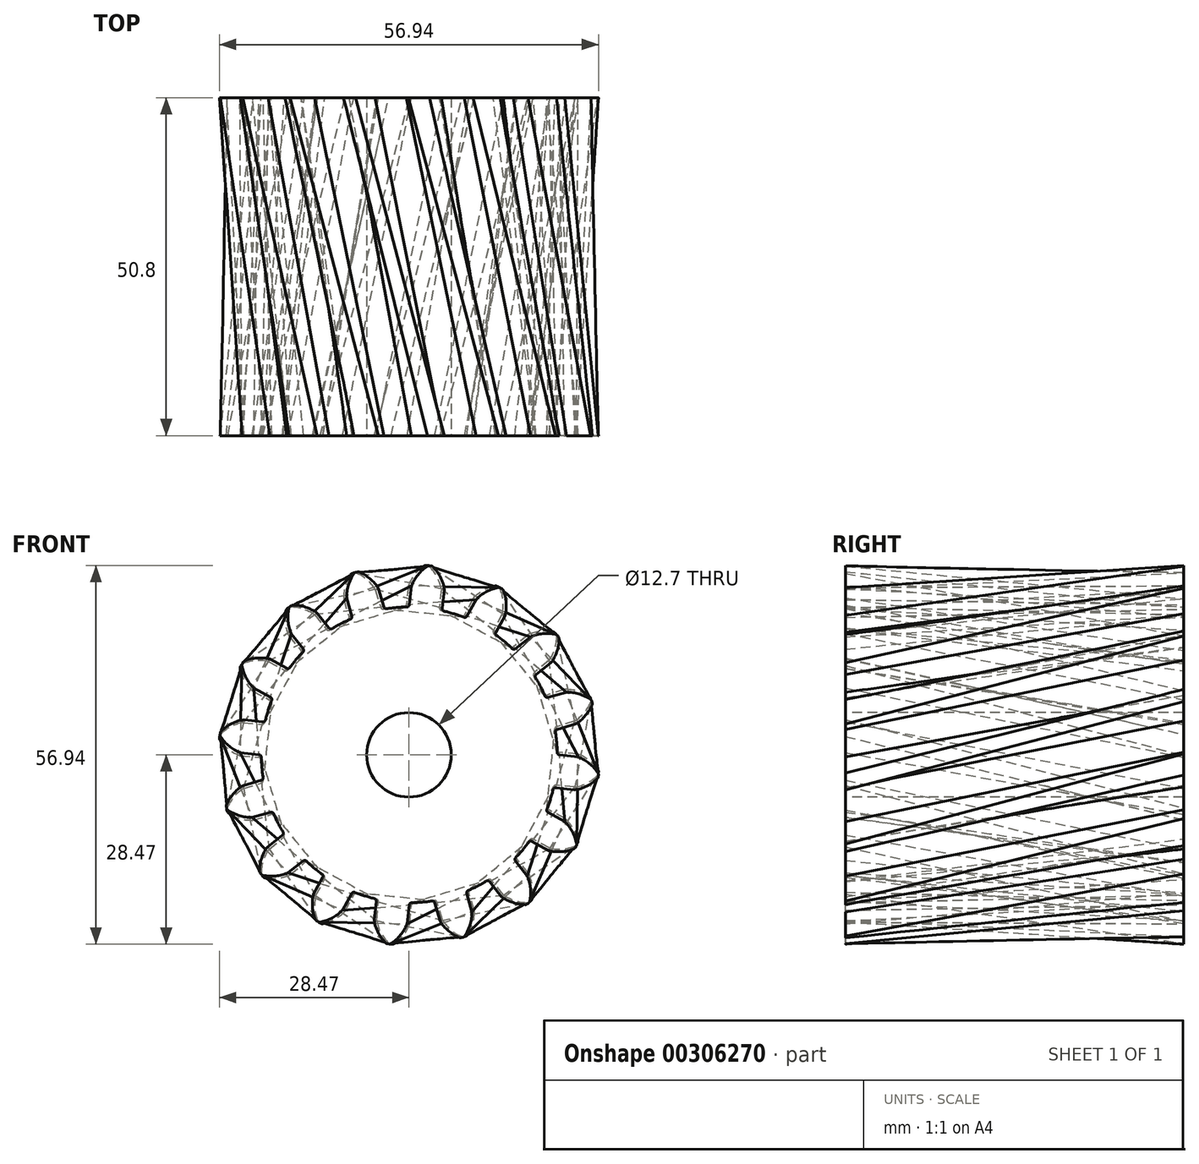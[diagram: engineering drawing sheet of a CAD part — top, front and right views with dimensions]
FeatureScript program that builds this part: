
annotation { "Feature Type Name" : "Feature", "Feature Type Description" : "" }
export const myFeature = defineFeature(function(context is Context, id is Id, definition is map)
    precondition{}
    {
        {
            var Q0;
            Q0=qCreatedBy(makeId("Front.planeOp"),FACE);
            var sketch = newSketch(context, id + "F0", { "sketchPlane" : qUnion([Q0])});
            skArc(sketch, "E0", {"start": v(-0.74, 22.21) * mm, "mid": v(-2.44, 22.1) * mm, "end": v(-4.12, 21.84) * mm});
            skArc(sketch, "E1.trimOffspring", {"start": v(4.85, 24.93) * mm, "mid": v(4.22, 26.77) * mm, "end": v(3.08, 28.32) * mm});
            skLineSegment(sketch, "E2", {"start": v(4.85, 24.93) * mm, "end": v(4.58, 22.1) * mm});
            skLineSegment(sketch, "E3", {"start": v(2.85, 28.43) * mm, "end": v(2.68, 28.45) * mm});
            skArc(sketch, "E4.MirrorCS", {"start": v(-0.11, 25.4) * mm, "mid": v(0.84, 27.08) * mm, "end": v(2.26, 28.4) * mm});
            skLineSegment(sketch, "E5.MirrorCS", {"start": v(2.5, 28.47) * mm, "end": v(2.68, 28.45) * mm});
            skLineSegment(sketch, "E6.MirrorCS", {"start": v(-0.11, 25.4) * mm, "end": v(-0.38, 22.56) * mm});
            skPoint(sketch, "E7.visualSharp", {"position": v(-0.4, 22.22) * mm});
            skArc(sketch, "E7.filletArc", {"start": v(-0.74, 22.21) * mm, "mid": v(-0.5, 22.32) * mm, "end": v(-0.38, 22.56) * mm});
            skPoint(sketch, "E8.visualSharp", {"position": v(4.55, 21.75) * mm});
            skArc(sketch, "E8.filletArc", {"start": v(4.58, 22.1) * mm, "mid": v(4.65, 21.83) * mm, "end": v(4.87, 21.68) * mm});
            skPoint(sketch, "E9.visualSharp", {"position": v(2.98, 28.42) * mm});
            skArc(sketch, "E9.filletArc", {"start": v(3.08, 28.32) * mm, "mid": v(2.97, 28.4) * mm, "end": v(2.85, 28.43) * mm});
            skPoint(sketch, "E10.visualSharp", {"position": v(2.37, 28.48) * mm});
            skArc(sketch, "E10.filletArc", {"start": v(2.5, 28.47) * mm, "mid": v(2.38, 28.45) * mm, "end": v(2.26, 28.4) * mm});
            skLineSegment(sketch, "E11.1.0", {"start": v(-9.82, 23.42) * mm, "end": v(-8.98, 20.7) * mm});
            skPoint(sketch, "E11.1.1", {"position": v(-8.88, 20.37) * mm});
            skLineSegment(sketch, "E11.1.2", {"start": v(-5.06, 24.9) * mm, "end": v(-4.22, 22.16) * mm});
            skPoint(sketch, "E11.1.3", {"position": v(-8.7, 27.22) * mm});
            skArc(sketch, "E11.1.4", {"start": v(-9.82, 23.42) * mm, "mid": v(-9.58, 25.34) * mm, "end": v(-8.78, 27.1) * mm});
            skPoint(sketch, "E11.1.5", {"position": v(-4.12, 21.84) * mm});
            skArc(sketch, "E11.1.6", {"start": v(-5.06, 24.9) * mm, "mid": v(-6.34, 26.34) * mm, "end": v(-8, 27.35) * mm});
            skPoint(sketch, "E11.1.7", {"position": v(-8.12, 27.4) * mm});
            skArc(sketch, "E11.1.8", {"start": v(-8.58, 27.26) * mm, "mid": v(-8.7, 27.2) * mm, "end": v(-8.78, 27.1) * mm});
            skLineSegment(sketch, "E11.1.9", {"start": v(-8.58, 27.26) * mm, "end": v(-8.41, 27.3) * mm});
            skArc(sketch, "E11.1.10", {"start": v(-9.19, 20.24) * mm, "mid": v(-9, 20.43) * mm, "end": v(-8.98, 20.7) * mm});
            skArc(sketch, "E11.1.11", {"start": v(-4.22, 22.16) * mm, "mid": v(-4.06, 21.95) * mm, "end": v(-3.8, 21.9) * mm});
            skLineSegment(sketch, "E11.1.12", {"start": v(-8.25, 27.36) * mm, "end": v(-8.41, 27.3) * mm});
            skArc(sketch, "E11.1.13", {"start": v(-8, 27.35) * mm, "mid": v(-8.12, 27.37) * mm, "end": v(-8.25, 27.36) * mm});
            skLineSegment(sketch, "E11.2.0", {"start": v(-18.04, 17.88) * mm, "end": v(-16.22, 15.68) * mm});
            skPoint(sketch, "E11.2.1", {"position": v(-16, 15.42) * mm});
            skLineSegment(sketch, "E11.2.2", {"start": v(-14.2, 21.06) * mm, "end": v(-12.38, 18.86) * mm});
            skPoint(sketch, "E11.2.3", {"position": v(-18.46, 21.81) * mm});
            skArc(sketch, "E11.2.4", {"start": v(-18.04, 17.88) * mm, "mid": v(-18.55, 19.75) * mm, "end": v(-18.48, 21.68) * mm});
            skPoint(sketch, "E11.2.5", {"position": v(-12.17, 18.6) * mm});
            skArc(sketch, "E11.2.6", {"start": v(-14.2, 21.06) * mm, "mid": v(-15.94, 21.91) * mm, "end": v(-17.85, 22.2) * mm});
            skPoint(sketch, "E11.2.7", {"position": v(-17.99, 22.2) * mm});
            skArc(sketch, "E11.2.8", {"start": v(-18.36, 21.9) * mm, "mid": v(-18.44, 21.8) * mm, "end": v(-18.48, 21.68) * mm});
            skLineSegment(sketch, "E11.2.9", {"start": v(-18.36, 21.9) * mm, "end": v(-18.23, 22.01) * mm});
            skArc(sketch, "E11.2.10", {"start": v(-16.23, 15.18) * mm, "mid": v(-16.13, 15.43) * mm, "end": v(-16.22, 15.68) * mm});
            skArc(sketch, "E11.2.11", {"start": v(-12.38, 18.86) * mm, "mid": v(-12.15, 18.73) * mm, "end": v(-11.89, 18.78) * mm});
            skLineSegment(sketch, "E11.2.12", {"start": v(-18.1, 22.12) * mm, "end": v(-18.23, 22.01) * mm});
            skArc(sketch, "E11.2.13", {"start": v(-17.85, 22.2) * mm, "mid": v(-17.98, 22.18) * mm, "end": v(-18.1, 22.12) * mm});
            skLineSegment(sketch, "E11.3.0", {"start": v(-23.5, 9.62) * mm, "end": v(-20.99, 8.28) * mm});
            skPoint(sketch, "E11.3.1", {"position": v(-20.69, 8.13) * mm});
            skLineSegment(sketch, "E11.3.2", {"start": v(-21.18, 14.02) * mm, "end": v(-18.66, 12.68) * mm});
            skPoint(sketch, "E11.3.3", {"position": v(-25.4, 13.1) * mm});
            skArc(sketch, "E11.3.4", {"start": v(-23.5, 9.62) * mm, "mid": v(-24.7, 11.14) * mm, "end": v(-25.37, 12.96) * mm});
            skPoint(sketch, "E11.3.5", {"position": v(-18.36, 12.53) * mm});
            skArc(sketch, "E11.3.6", {"start": v(-21.18, 14.02) * mm, "mid": v(-23.11, 14.14) * mm, "end": v(-25, 13.68) * mm});
            skPoint(sketch, "E11.3.7", {"position": v(-25.12, 13.63) * mm});
            skArc(sketch, "E11.3.8", {"start": v(-25.34, 13.2) * mm, "mid": v(-25.38, 13.09) * mm, "end": v(-25.37, 12.96) * mm});
            skLineSegment(sketch, "E11.3.9", {"start": v(-25.34, 13.2) * mm, "end": v(-25.26, 13.36) * mm});
            skArc(sketch, "E11.3.10", {"start": v(-20.8, 7.81) * mm, "mid": v(-20.8, 8.08) * mm, "end": v(-20.99, 8.28) * mm});
            skArc(sketch, "E11.3.11", {"start": v(-18.66, 12.68) * mm, "mid": v(-18.4, 12.65) * mm, "end": v(-18.17, 12.8) * mm});
            skLineSegment(sketch, "E11.3.12", {"start": v(-25.18, 13.51) * mm, "end": v(-25.26, 13.36) * mm});
            skArc(sketch, "E11.3.13", {"start": v(-25, 13.68) * mm, "mid": v(-25.1, 13.61) * mm, "end": v(-25.18, 13.51) * mm});
            skLineSegment(sketch, "E11.4.0", {"start": v(-25.4, -0.11) * mm, "end": v(-22.56, -0.38) * mm});
            skPoint(sketch, "E11.4.1", {"position": v(-22.22, -0.4) * mm});
            skLineSegment(sketch, "E11.4.2", {"start": v(-24.93, 4.85) * mm, "end": v(-22.1, 4.58) * mm});
            skPoint(sketch, "E11.4.3", {"position": v(-28.48, 2.37) * mm});
            skArc(sketch, "E11.4.4", {"start": v(-25.4, -0.11) * mm, "mid": v(-27.08, 0.84) * mm, "end": v(-28.4, 2.26) * mm});
            skPoint(sketch, "E11.4.5", {"position": v(-21.75, 4.55) * mm});
            skArc(sketch, "E11.4.6", {"start": v(-24.93, 4.85) * mm, "mid": v(-26.77, 4.22) * mm, "end": v(-28.32, 3.08) * mm});
            skPoint(sketch, "E11.4.7", {"position": v(-28.42, 2.98) * mm});
            skArc(sketch, "E11.4.8", {"start": v(-28.47, 2.5) * mm, "mid": v(-28.45, 2.38) * mm, "end": v(-28.4, 2.26) * mm});
            skLineSegment(sketch, "E11.4.9", {"start": v(-28.47, 2.5) * mm, "end": v(-28.45, 2.68) * mm});
            skArc(sketch, "E11.4.10", {"start": v(-22.21, -0.74) * mm, "mid": v(-22.32, -0.5) * mm, "end": v(-22.56, -0.38) * mm});
            skArc(sketch, "E11.4.11", {"start": v(-22.1, 4.58) * mm, "mid": v(-21.83, 4.65) * mm, "end": v(-21.68, 4.87) * mm});
            skLineSegment(sketch, "E11.4.12", {"start": v(-28.43, 2.85) * mm, "end": v(-28.45, 2.68) * mm});
            skArc(sketch, "E11.4.13", {"start": v(-28.32, 3.08) * mm, "mid": v(-28.4, 2.97) * mm, "end": v(-28.43, 2.85) * mm});
            skLineSegment(sketch, "E11.5.0", {"start": v(-23.42, -9.82) * mm, "end": v(-20.7, -8.98) * mm});
            skPoint(sketch, "E11.5.1", {"position": v(-20.37, -8.88) * mm});
            skLineSegment(sketch, "E11.5.2", {"start": v(-24.9, -5.06) * mm, "end": v(-22.16, -4.22) * mm});
            skPoint(sketch, "E11.5.3", {"position": v(-27.22, -8.7) * mm});
            skArc(sketch, "E11.5.4", {"start": v(-23.42, -9.82) * mm, "mid": v(-25.34, -9.58) * mm, "end": v(-27.1, -8.78) * mm});
            skPoint(sketch, "E11.5.5", {"position": v(-21.84, -4.12) * mm});
            skArc(sketch, "E11.5.6", {"start": v(-24.9, -5.06) * mm, "mid": v(-26.34, -6.34) * mm, "end": v(-27.35, -8) * mm});
            skPoint(sketch, "E11.5.7", {"position": v(-27.4, -8.12) * mm});
            skArc(sketch, "E11.5.8", {"start": v(-27.26, -8.58) * mm, "mid": v(-27.2, -8.7) * mm, "end": v(-27.1, -8.78) * mm});
            skLineSegment(sketch, "E11.5.9", {"start": v(-27.26, -8.58) * mm, "end": v(-27.3, -8.41) * mm});
            skArc(sketch, "E11.5.10", {"start": v(-20.24, -9.19) * mm, "mid": v(-20.43, -9) * mm, "end": v(-20.7, -8.98) * mm});
            skArc(sketch, "E11.5.11", {"start": v(-22.16, -4.22) * mm, "mid": v(-21.95, -4.06) * mm, "end": v(-21.9, -3.8) * mm});
            skLineSegment(sketch, "E11.5.12", {"start": v(-27.36, -8.25) * mm, "end": v(-27.3, -8.41) * mm});
            skArc(sketch, "E11.5.13", {"start": v(-27.35, -8) * mm, "mid": v(-27.37, -8.12) * mm, "end": v(-27.36, -8.25) * mm});
            skLineSegment(sketch, "E11.6.0", {"start": v(-17.88, -18.04) * mm, "end": v(-15.68, -16.22) * mm});
            skPoint(sketch, "E11.6.1", {"position": v(-15.42, -16) * mm});
            skLineSegment(sketch, "E11.6.2", {"start": v(-21.06, -14.2) * mm, "end": v(-18.86, -12.38) * mm});
            skPoint(sketch, "E11.6.3", {"position": v(-21.81, -18.46) * mm});
            skArc(sketch, "E11.6.4", {"start": v(-17.88, -18.04) * mm, "mid": v(-19.75, -18.55) * mm, "end": v(-21.68, -18.48) * mm});
            skPoint(sketch, "E11.6.5", {"position": v(-18.6, -12.17) * mm});
            skArc(sketch, "E11.6.6", {"start": v(-21.06, -14.2) * mm, "mid": v(-21.91, -15.94) * mm, "end": v(-22.2, -17.85) * mm});
            skPoint(sketch, "E11.6.7", {"position": v(-22.2, -17.99) * mm});
            skArc(sketch, "E11.6.8", {"start": v(-21.9, -18.36) * mm, "mid": v(-21.8, -18.44) * mm, "end": v(-21.68, -18.48) * mm});
            skLineSegment(sketch, "E11.6.9", {"start": v(-21.9, -18.36) * mm, "end": v(-22.01, -18.23) * mm});
            skArc(sketch, "E11.6.10", {"start": v(-15.18, -16.23) * mm, "mid": v(-15.43, -16.13) * mm, "end": v(-15.68, -16.22) * mm});
            skArc(sketch, "E11.6.11", {"start": v(-18.86, -12.38) * mm, "mid": v(-18.73, -12.15) * mm, "end": v(-18.78, -11.89) * mm});
            skLineSegment(sketch, "E11.6.12", {"start": v(-22.12, -18.1) * mm, "end": v(-22.01, -18.23) * mm});
            skArc(sketch, "E11.6.13", {"start": v(-22.2, -17.85) * mm, "mid": v(-22.18, -17.98) * mm, "end": v(-22.12, -18.1) * mm});
            skLineSegment(sketch, "E11.7.0", {"start": v(-9.62, -23.5) * mm, "end": v(-8.28, -20.99) * mm});
            skPoint(sketch, "E11.7.1", {"position": v(-8.13, -20.69) * mm});
            skLineSegment(sketch, "E11.7.2", {"start": v(-14.02, -21.18) * mm, "end": v(-12.68, -18.66) * mm});
            skPoint(sketch, "E11.7.3", {"position": v(-13.1, -25.4) * mm});
            skArc(sketch, "E11.7.4", {"start": v(-9.62, -23.5) * mm, "mid": v(-11.14, -24.7) * mm, "end": v(-12.96, -25.37) * mm});
            skPoint(sketch, "E11.7.5", {"position": v(-12.53, -18.36) * mm});
            skArc(sketch, "E11.7.6", {"start": v(-14.02, -21.18) * mm, "mid": v(-14.14, -23.11) * mm, "end": v(-13.68, -25) * mm});
            skPoint(sketch, "E11.7.7", {"position": v(-13.63, -25.12) * mm});
            skArc(sketch, "E11.7.8", {"start": v(-13.2, -25.34) * mm, "mid": v(-13.09, -25.38) * mm, "end": v(-12.96, -25.37) * mm});
            skLineSegment(sketch, "E11.7.9", {"start": v(-13.2, -25.34) * mm, "end": v(-13.36, -25.26) * mm});
            skArc(sketch, "E11.7.10", {"start": v(-7.81, -20.8) * mm, "mid": v(-8.08, -20.8) * mm, "end": v(-8.28, -20.99) * mm});
            skArc(sketch, "E11.7.11", {"start": v(-12.68, -18.66) * mm, "mid": v(-12.65, -18.4) * mm, "end": v(-12.8, -18.17) * mm});
            skLineSegment(sketch, "E11.7.12", {"start": v(-13.51, -25.18) * mm, "end": v(-13.36, -25.26) * mm});
            skArc(sketch, "E11.7.13", {"start": v(-13.68, -25) * mm, "mid": v(-13.61, -25.1) * mm, "end": v(-13.51, -25.18) * mm});
            skLineSegment(sketch, "E11.8.0", {"start": v(0.11, -25.4) * mm, "end": v(0.38, -22.56) * mm});
            skPoint(sketch, "E11.8.1", {"position": v(0.4, -22.22) * mm});
            skLineSegment(sketch, "E11.8.2", {"start": v(-4.85, -24.93) * mm, "end": v(-4.58, -22.1) * mm});
            skPoint(sketch, "E11.8.3", {"position": v(-2.37, -28.48) * mm});
            skArc(sketch, "E11.8.4", {"start": v(0.11, -25.4) * mm, "mid": v(-0.84, -27.08) * mm, "end": v(-2.26, -28.4) * mm});
            skPoint(sketch, "E11.8.5", {"position": v(-4.55, -21.75) * mm});
            skArc(sketch, "E11.8.6", {"start": v(-4.85, -24.93) * mm, "mid": v(-4.22, -26.77) * mm, "end": v(-3.08, -28.32) * mm});
            skPoint(sketch, "E11.8.7", {"position": v(-2.98, -28.42) * mm});
            skArc(sketch, "E11.8.8", {"start": v(-2.5, -28.47) * mm, "mid": v(-2.38, -28.45) * mm, "end": v(-2.26, -28.4) * mm});
            skLineSegment(sketch, "E11.8.9", {"start": v(-2.5, -28.47) * mm, "end": v(-2.68, -28.45) * mm});
            skArc(sketch, "E11.8.10", {"start": v(0.74, -22.21) * mm, "mid": v(0.5, -22.32) * mm, "end": v(0.38, -22.56) * mm});
            skArc(sketch, "E11.8.11", {"start": v(-4.58, -22.1) * mm, "mid": v(-4.65, -21.83) * mm, "end": v(-4.87, -21.68) * mm});
            skLineSegment(sketch, "E11.8.12", {"start": v(-2.85, -28.43) * mm, "end": v(-2.68, -28.45) * mm});
            skArc(sketch, "E11.8.13", {"start": v(-3.08, -28.32) * mm, "mid": v(-2.97, -28.4) * mm, "end": v(-2.85, -28.43) * mm});
            skLineSegment(sketch, "E11.9.0", {"start": v(9.82, -23.42) * mm, "end": v(8.98, -20.7) * mm});
            skPoint(sketch, "E11.9.1", {"position": v(8.88, -20.37) * mm});
            skLineSegment(sketch, "E11.9.2", {"start": v(5.06, -24.9) * mm, "end": v(4.22, -22.16) * mm});
            skPoint(sketch, "E11.9.3", {"position": v(8.7, -27.22) * mm});
            skArc(sketch, "E11.9.4", {"start": v(9.82, -23.42) * mm, "mid": v(9.58, -25.34) * mm, "end": v(8.78, -27.1) * mm});
            skPoint(sketch, "E11.9.5", {"position": v(4.12, -21.84) * mm});
            skArc(sketch, "E11.9.6", {"start": v(5.06, -24.9) * mm, "mid": v(6.34, -26.34) * mm, "end": v(8, -27.35) * mm});
            skPoint(sketch, "E11.9.7", {"position": v(8.12, -27.4) * mm});
            skArc(sketch, "E11.9.8", {"start": v(8.58, -27.26) * mm, "mid": v(8.7, -27.2) * mm, "end": v(8.78, -27.1) * mm});
            skLineSegment(sketch, "E11.9.9", {"start": v(8.58, -27.26) * mm, "end": v(8.41, -27.3) * mm});
            skArc(sketch, "E11.9.10", {"start": v(9.19, -20.24) * mm, "mid": v(9, -20.43) * mm, "end": v(8.98, -20.7) * mm});
            skArc(sketch, "E11.9.11", {"start": v(4.22, -22.16) * mm, "mid": v(4.06, -21.95) * mm, "end": v(3.8, -21.9) * mm});
            skLineSegment(sketch, "E11.9.12", {"start": v(8.25, -27.36) * mm, "end": v(8.41, -27.3) * mm});
            skArc(sketch, "E11.9.13", {"start": v(8, -27.35) * mm, "mid": v(8.12, -27.37) * mm, "end": v(8.25, -27.36) * mm});
            skLineSegment(sketch, "E11.10.0", {"start": v(18.04, -17.88) * mm, "end": v(16.22, -15.68) * mm});
            skPoint(sketch, "E11.10.1", {"position": v(16, -15.42) * mm});
            skLineSegment(sketch, "E11.10.2", {"start": v(14.2, -21.06) * mm, "end": v(12.38, -18.86) * mm});
            skPoint(sketch, "E11.10.3", {"position": v(18.46, -21.81) * mm});
            skArc(sketch, "E11.10.4", {"start": v(18.04, -17.88) * mm, "mid": v(18.55, -19.75) * mm, "end": v(18.48, -21.68) * mm});
            skPoint(sketch, "E11.10.5", {"position": v(12.17, -18.6) * mm});
            skArc(sketch, "E11.10.6", {"start": v(14.2, -21.06) * mm, "mid": v(15.94, -21.91) * mm, "end": v(17.85, -22.2) * mm});
            skPoint(sketch, "E11.10.7", {"position": v(17.99, -22.2) * mm});
            skArc(sketch, "E11.10.8", {"start": v(18.36, -21.9) * mm, "mid": v(18.44, -21.8) * mm, "end": v(18.48, -21.68) * mm});
            skLineSegment(sketch, "E11.10.9", {"start": v(18.36, -21.9) * mm, "end": v(18.23, -22.01) * mm});
            skArc(sketch, "E11.10.10", {"start": v(16.23, -15.18) * mm, "mid": v(16.13, -15.43) * mm, "end": v(16.22, -15.68) * mm});
            skArc(sketch, "E11.10.11", {"start": v(12.38, -18.86) * mm, "mid": v(12.15, -18.73) * mm, "end": v(11.89, -18.78) * mm});
            skLineSegment(sketch, "E11.10.12", {"start": v(18.1, -22.12) * mm, "end": v(18.23, -22.01) * mm});
            skArc(sketch, "E11.10.13", {"start": v(17.85, -22.2) * mm, "mid": v(17.98, -22.18) * mm, "end": v(18.1, -22.12) * mm});
            skLineSegment(sketch, "E11.11.0", {"start": v(23.5, -9.62) * mm, "end": v(20.99, -8.28) * mm});
            skPoint(sketch, "E11.11.1", {"position": v(20.69, -8.13) * mm});
            skLineSegment(sketch, "E11.11.2", {"start": v(21.18, -14.02) * mm, "end": v(18.66, -12.68) * mm});
            skPoint(sketch, "E11.11.3", {"position": v(25.4, -13.1) * mm});
            skArc(sketch, "E11.11.4", {"start": v(23.5, -9.62) * mm, "mid": v(24.7, -11.14) * mm, "end": v(25.37, -12.96) * mm});
            skPoint(sketch, "E11.11.5", {"position": v(18.36, -12.53) * mm});
            skArc(sketch, "E11.11.6", {"start": v(21.18, -14.02) * mm, "mid": v(23.11, -14.14) * mm, "end": v(25, -13.68) * mm});
            skPoint(sketch, "E11.11.7", {"position": v(25.12, -13.63) * mm});
            skArc(sketch, "E11.11.8", {"start": v(25.34, -13.2) * mm, "mid": v(25.38, -13.09) * mm, "end": v(25.37, -12.96) * mm});
            skLineSegment(sketch, "E11.11.9", {"start": v(25.34, -13.2) * mm, "end": v(25.26, -13.36) * mm});
            skArc(sketch, "E11.11.10", {"start": v(20.8, -7.81) * mm, "mid": v(20.8, -8.08) * mm, "end": v(20.99, -8.28) * mm});
            skArc(sketch, "E11.11.11", {"start": v(18.66, -12.68) * mm, "mid": v(18.4, -12.65) * mm, "end": v(18.17, -12.8) * mm});
            skLineSegment(sketch, "E11.11.12", {"start": v(25.18, -13.51) * mm, "end": v(25.26, -13.36) * mm});
            skArc(sketch, "E11.11.13", {"start": v(25, -13.68) * mm, "mid": v(25.1, -13.61) * mm, "end": v(25.18, -13.51) * mm});
            skLineSegment(sketch, "E11.12.0", {"start": v(25.4, 0.11) * mm, "end": v(22.56, 0.38) * mm});
            skPoint(sketch, "E11.12.1", {"position": v(22.22, 0.4) * mm});
            skLineSegment(sketch, "E11.12.2", {"start": v(24.93, -4.85) * mm, "end": v(22.1, -4.58) * mm});
            skPoint(sketch, "E11.12.3", {"position": v(28.48, -2.37) * mm});
            skArc(sketch, "E11.12.4", {"start": v(25.4, 0.11) * mm, "mid": v(27.08, -0.84) * mm, "end": v(28.4, -2.26) * mm});
            skPoint(sketch, "E11.12.5", {"position": v(21.75, -4.55) * mm});
            skArc(sketch, "E11.12.6", {"start": v(24.93, -4.85) * mm, "mid": v(26.77, -4.22) * mm, "end": v(28.32, -3.08) * mm});
            skPoint(sketch, "E11.12.7", {"position": v(28.42, -2.98) * mm});
            skArc(sketch, "E11.12.8", {"start": v(28.47, -2.5) * mm, "mid": v(28.45, -2.38) * mm, "end": v(28.4, -2.26) * mm});
            skLineSegment(sketch, "E11.12.9", {"start": v(28.47, -2.5) * mm, "end": v(28.45, -2.68) * mm});
            skArc(sketch, "E11.12.10", {"start": v(22.21, 0.74) * mm, "mid": v(22.32, 0.5) * mm, "end": v(22.56, 0.38) * mm});
            skArc(sketch, "E11.12.11", {"start": v(22.1, -4.58) * mm, "mid": v(21.83, -4.65) * mm, "end": v(21.68, -4.87) * mm});
            skLineSegment(sketch, "E11.12.12", {"start": v(28.43, -2.85) * mm, "end": v(28.45, -2.68) * mm});
            skArc(sketch, "E11.12.13", {"start": v(28.32, -3.08) * mm, "mid": v(28.4, -2.97) * mm, "end": v(28.43, -2.85) * mm});
            skLineSegment(sketch, "E11.13.0", {"start": v(23.42, 9.82) * mm, "end": v(20.7, 8.98) * mm});
            skPoint(sketch, "E11.13.1", {"position": v(20.37, 8.88) * mm});
            skLineSegment(sketch, "E11.13.2", {"start": v(24.9, 5.06) * mm, "end": v(22.16, 4.22) * mm});
            skPoint(sketch, "E11.13.3", {"position": v(27.22, 8.7) * mm});
            skArc(sketch, "E11.13.4", {"start": v(23.42, 9.82) * mm, "mid": v(25.34, 9.58) * mm, "end": v(27.1, 8.78) * mm});
            skPoint(sketch, "E11.13.5", {"position": v(21.84, 4.12) * mm});
            skArc(sketch, "E11.13.6", {"start": v(24.9, 5.06) * mm, "mid": v(26.34, 6.34) * mm, "end": v(27.35, 8) * mm});
            skPoint(sketch, "E11.13.7", {"position": v(27.4, 8.12) * mm});
            skArc(sketch, "E11.13.8", {"start": v(27.26, 8.58) * mm, "mid": v(27.2, 8.7) * mm, "end": v(27.1, 8.78) * mm});
            skLineSegment(sketch, "E11.13.9", {"start": v(27.26, 8.58) * mm, "end": v(27.3, 8.41) * mm});
            skArc(sketch, "E11.13.10", {"start": v(20.24, 9.19) * mm, "mid": v(20.43, 9) * mm, "end": v(20.7, 8.98) * mm});
            skArc(sketch, "E11.13.11", {"start": v(22.16, 4.22) * mm, "mid": v(21.95, 4.06) * mm, "end": v(21.9, 3.8) * mm});
            skLineSegment(sketch, "E11.13.12", {"start": v(27.36, 8.25) * mm, "end": v(27.3, 8.41) * mm});
            skArc(sketch, "E11.13.13", {"start": v(27.35, 8) * mm, "mid": v(27.37, 8.12) * mm, "end": v(27.36, 8.25) * mm});
            skLineSegment(sketch, "E11.14.0", {"start": v(17.88, 18.04) * mm, "end": v(15.68, 16.22) * mm});
            skPoint(sketch, "E11.14.1", {"position": v(15.42, 16) * mm});
            skLineSegment(sketch, "E11.14.2", {"start": v(21.06, 14.2) * mm, "end": v(18.86, 12.38) * mm});
            skPoint(sketch, "E11.14.3", {"position": v(21.81, 18.46) * mm});
            skArc(sketch, "E11.14.4", {"start": v(17.88, 18.04) * mm, "mid": v(19.75, 18.55) * mm, "end": v(21.68, 18.48) * mm});
            skPoint(sketch, "E11.14.5", {"position": v(18.6, 12.17) * mm});
            skArc(sketch, "E11.14.6", {"start": v(21.06, 14.2) * mm, "mid": v(21.91, 15.94) * mm, "end": v(22.2, 17.85) * mm});
            skPoint(sketch, "E11.14.7", {"position": v(22.2, 17.99) * mm});
            skArc(sketch, "E11.14.8", {"start": v(21.9, 18.36) * mm, "mid": v(21.8, 18.44) * mm, "end": v(21.68, 18.48) * mm});
            skLineSegment(sketch, "E11.14.9", {"start": v(21.9, 18.36) * mm, "end": v(22.01, 18.23) * mm});
            skArc(sketch, "E11.14.10", {"start": v(15.18, 16.23) * mm, "mid": v(15.43, 16.13) * mm, "end": v(15.68, 16.22) * mm});
            skArc(sketch, "E11.14.11", {"start": v(18.86, 12.38) * mm, "mid": v(18.73, 12.15) * mm, "end": v(18.78, 11.89) * mm});
            skLineSegment(sketch, "E11.14.12", {"start": v(22.12, 18.1) * mm, "end": v(22.01, 18.23) * mm});
            skArc(sketch, "E11.14.13", {"start": v(22.2, 17.85) * mm, "mid": v(22.18, 17.98) * mm, "end": v(22.12, 18.1) * mm});
            skLineSegment(sketch, "E11.15.0", {"start": v(9.62, 23.5) * mm, "end": v(8.28, 20.99) * mm});
            skPoint(sketch, "E11.15.1", {"position": v(8.13, 20.69) * mm});
            skLineSegment(sketch, "E11.15.2", {"start": v(14.02, 21.18) * mm, "end": v(12.68, 18.66) * mm});
            skPoint(sketch, "E11.15.3", {"position": v(13.1, 25.4) * mm});
            skArc(sketch, "E11.15.4", {"start": v(9.62, 23.5) * mm, "mid": v(11.14, 24.7) * mm, "end": v(12.96, 25.37) * mm});
            skPoint(sketch, "E11.15.5", {"position": v(12.53, 18.36) * mm});
            skArc(sketch, "E11.15.6", {"start": v(14.02, 21.18) * mm, "mid": v(14.14, 23.11) * mm, "end": v(13.68, 25) * mm});
            skPoint(sketch, "E11.15.7", {"position": v(13.63, 25.12) * mm});
            skArc(sketch, "E11.15.8", {"start": v(13.2, 25.34) * mm, "mid": v(13.09, 25.38) * mm, "end": v(12.96, 25.37) * mm});
            skLineSegment(sketch, "E11.15.9", {"start": v(13.2, 25.34) * mm, "end": v(13.36, 25.26) * mm});
            skArc(sketch, "E11.15.10", {"start": v(7.81, 20.8) * mm, "mid": v(8.08, 20.8) * mm, "end": v(8.28, 20.99) * mm});
            skArc(sketch, "E11.15.11", {"start": v(12.68, 18.66) * mm, "mid": v(12.65, 18.4) * mm, "end": v(12.8, 18.17) * mm});
            skLineSegment(sketch, "E11.15.12", {"start": v(13.51, 25.18) * mm, "end": v(13.36, 25.26) * mm});
            skArc(sketch, "E11.15.13", {"start": v(13.68, 25) * mm, "mid": v(13.61, 25.1) * mm, "end": v(13.51, 25.18) * mm});
            skArc(sketch, "E12.trimOffspring", {"start": v(8.13, 20.69) * mm, "mid": v(6.52, 21.25) * mm, "end": v(4.87, 21.68) * mm});
            skArc(sketch, "E13.trimOffspring", {"start": v(-8.88, 20.37) * mm, "mid": v(-10.56, 19.55) * mm, "end": v(-12.17, 18.6) * mm});
            skArc(sketch, "E14.trimOffspring", {"start": v(15.42, 16) * mm, "mid": v(14.02, 17.24) * mm, "end": v(12.53, 18.36) * mm});
            skArc(sketch, "E15.trimOffspring", {"start": v(-16, 15.42) * mm, "mid": v(-17.24, 14.02) * mm, "end": v(-18.36, 12.53) * mm});
            skArc(sketch, "E16.trimOffspring", {"start": v(-20.69, 8.13) * mm, "mid": v(-21.25, 6.52) * mm, "end": v(-21.68, 4.87) * mm});
            skArc(sketch, "E17.trimOffspring", {"start": v(20.37, 8.88) * mm, "mid": v(19.55, 10.56) * mm, "end": v(18.6, 12.17) * mm});
            skArc(sketch, "E18.trimOffspring", {"start": v(22.22, 0.4) * mm, "mid": v(22.1, 2.27) * mm, "end": v(21.84, 4.12) * mm});
            skArc(sketch, "E19.trimOffspring", {"start": v(-22.22, -0.4) * mm, "mid": v(-22.12, -2.1) * mm, "end": v(-21.9, -3.8) * mm});
            skArc(sketch, "E20.trimOffspring", {"start": v(-20.37, -8.88) * mm, "mid": v(-19.55, -10.56) * mm, "end": v(-18.6, -12.17) * mm});
            skArc(sketch, "E21.trimOffspring", {"start": v(-8.13, -20.69) * mm, "mid": v(-6.36, -21.3) * mm, "end": v(-4.55, -21.75) * mm});
            skArc(sketch, "E22.trimOffspring", {"start": v(-15.42, -16) * mm, "mid": v(-14.02, -17.24) * mm, "end": v(-12.53, -18.36) * mm});
            skArc(sketch, "E23.trimOffspring", {"start": v(0.4, -22.22) * mm, "mid": v(2.1, -22.12) * mm, "end": v(3.8, -21.9) * mm});
            skArc(sketch, "E24.trimOffspring", {"start": v(8.88, -20.37) * mm, "mid": v(10.41, -19.63) * mm, "end": v(11.89, -18.78) * mm});
            skArc(sketch, "E25.trimOffspring", {"start": v(16, -15.42) * mm, "mid": v(17.24, -14.02) * mm, "end": v(18.36, -12.53) * mm});
            skArc(sketch, "E26.trimOffspring", {"start": v(20.69, -8.13) * mm, "mid": v(21.3, -6.36) * mm, "end": v(21.75, -4.55) * mm});
            skSolve(sketch);
        }
        {
            var Q0;
            Q0=makeQuery(id+"F0.imprint","IMPRINT",FACE,{"disambiguationData":[TD([[makeQuery(id+"F0.imprint","IMPRINT",EDGE,{"derivedFrom":sQuery(id+"F0.wireOp",EDGE,"E1.trimOffspring")}),1.0]])]});
            cPlane(context, id + "F1", {"entities" : qUnion([Q0]), "cplaneType" : CPlaneType.OFFSET, "offset" : 50.8 * mm, "width" : 152.4 * mm, "height" : 152.4 * mm});
        }
        {
            var Q0;
            Q0=qCreatedBy(id+"F1.planeOp",FACE);
            var sketch = newSketch(context, id + "F2", { "sketchPlane" : qUnion([Q0])});
            skArc(sketch, "E27", {"start": v(-15.92, 15.46) * mm, "mid": v(-17.06, 14.2) * mm, "end": v(-18.1, 12.85) * mm});
            skArc(sketch, "E28.trimOffspring", {"start": v(-13.79, 21.3) * mm, "mid": v(-15.5, 22.19) * mm, "end": v(-17.42, 22.51) * mm});
            skLineSegment(sketch, "E29", {"start": v(-13.79, 21.3) * mm, "end": v(-12, 19.07) * mm});
            skLineSegment(sketch, "E30", {"start": v(-17.66, 22.43) * mm, "end": v(-17.8, 22.33) * mm});
            skArc(sketch, "E31.MirrorCS", {"start": v(-17.68, 18.2) * mm, "mid": v(-18.16, 20.07) * mm, "end": v(-18.06, 22) * mm});
            skLineSegment(sketch, "E32.MirrorCS", {"start": v(-17.92, 22.22) * mm, "end": v(-17.8, 22.33) * mm});
            skLineSegment(sketch, "E33.MirrorCS", {"start": v(-17.68, 18.2) * mm, "end": v(-15.9, 15.96) * mm});
            skPoint(sketch, "E34.visualSharp", {"position": v(-15.68, 15.7) * mm});
            skArc(sketch, "E34.filletArc", {"start": v(-15.92, 15.46) * mm, "mid": v(-15.81, 15.7) * mm, "end": v(-15.9, 15.96) * mm});
            skPoint(sketch, "E35.visualSharp", {"position": v(-11.8, 18.8) * mm});
            skArc(sketch, "E35.filletArc", {"start": v(-12, 19.07) * mm, "mid": v(-11.77, 18.93) * mm, "end": v(-11.5, 18.98) * mm});
            skPoint(sketch, "E36.visualSharp", {"position": v(-17.55, 22.51) * mm});
            skArc(sketch, "E36.filletArc", {"start": v(-17.42, 22.51) * mm, "mid": v(-17.54, 22.5) * mm, "end": v(-17.66, 22.43) * mm});
            skPoint(sketch, "E37.visualSharp", {"position": v(-18.03, 22.13) * mm});
            skArc(sketch, "E37.filletArc", {"start": v(-17.92, 22.22) * mm, "mid": v(-18, 22.12) * mm, "end": v(-18.06, 22) * mm});
            skLineSegment(sketch, "E38.1.0", {"start": v(-23.3, 10.03) * mm, "end": v(-20.8, 8.65) * mm});
            skPoint(sketch, "E38.1.1", {"position": v(-20.5, 8.48) * mm});
            skLineSegment(sketch, "E38.1.2", {"start": v(-20.89, 14.39) * mm, "end": v(-18.39, 13) * mm});
            skPoint(sketch, "E38.1.3", {"position": v(-25.12, 13.53) * mm});
            skArc(sketch, "E38.1.4", {"start": v(-23.3, 10.03) * mm, "mid": v(-24.45, 11.57) * mm, "end": v(-25.1, 13.4) * mm});
            skPoint(sketch, "E38.1.5", {"position": v(-18.1, 12.85) * mm});
            skArc(sketch, "E38.1.6", {"start": v(-20.89, 14.39) * mm, "mid": v(-22.81, 14.55) * mm, "end": v(-24.7, 14.12) * mm});
            skPoint(sketch, "E38.1.7", {"position": v(-24.83, 14.06) * mm});
            skArc(sketch, "E38.1.8", {"start": v(-25.06, 13.65) * mm, "mid": v(-25.1, 13.53) * mm, "end": v(-25.1, 13.4) * mm});
            skLineSegment(sketch, "E38.1.9", {"start": v(-25.06, 13.65) * mm, "end": v(-24.98, 13.8) * mm});
            skArc(sketch, "E38.1.10", {"start": v(-20.62, 8.17) * mm, "mid": v(-20.62, 8.44) * mm, "end": v(-20.8, 8.65) * mm});
            skArc(sketch, "E38.1.11", {"start": v(-18.39, 13) * mm, "mid": v(-18.12, 12.97) * mm, "end": v(-17.9, 13.12) * mm});
            skLineSegment(sketch, "E38.1.12", {"start": v(-24.9, 13.95) * mm, "end": v(-24.98, 13.8) * mm});
            skArc(sketch, "E38.1.13", {"start": v(-24.7, 14.12) * mm, "mid": v(-24.81, 14.05) * mm, "end": v(-24.9, 13.95) * mm});
            skLineSegment(sketch, "E38.2.0", {"start": v(-25.35, 0.33) * mm, "end": v(-22.51, 0.02) * mm});
            skPoint(sketch, "E38.2.1", {"position": v(-22.18, -0.02) * mm});
            skLineSegment(sketch, "E38.2.2", {"start": v(-24.8, 5.28) * mm, "end": v(-21.96, 4.96) * mm});
            skPoint(sketch, "E38.2.3", {"position": v(-28.38, 2.87) * mm});
            skArc(sketch, "E38.2.4", {"start": v(-25.35, 0.33) * mm, "mid": v(-27.02, 1.32) * mm, "end": v(-28.31, 2.76) * mm});
            skPoint(sketch, "E38.2.5", {"position": v(-21.63, 4.93) * mm});
            skArc(sketch, "E38.2.6", {"start": v(-24.8, 5.28) * mm, "mid": v(-26.64, 4.69) * mm, "end": v(-28.22, 3.57) * mm});
            skPoint(sketch, "E38.2.7", {"position": v(-28.32, 3.47) * mm});
            skArc(sketch, "E38.2.8", {"start": v(-28.37, 3) * mm, "mid": v(-28.36, 2.87) * mm, "end": v(-28.31, 2.76) * mm});
            skLineSegment(sketch, "E38.2.9", {"start": v(-28.37, 3) * mm, "end": v(-28.35, 3.17) * mm});
            skArc(sketch, "E38.2.10", {"start": v(-22.18, -0.36) * mm, "mid": v(-22.27, -0.1) * mm, "end": v(-22.51, 0.02) * mm});
            skArc(sketch, "E38.2.11", {"start": v(-21.96, 4.96) * mm, "mid": v(-21.7, 5.03) * mm, "end": v(-21.55, 5.25) * mm});
            skLineSegment(sketch, "E38.2.12", {"start": v(-28.33, 3.34) * mm, "end": v(-28.35, 3.17) * mm});
            skArc(sketch, "E38.2.13", {"start": v(-28.22, 3.57) * mm, "mid": v(-28.3, 3.47) * mm, "end": v(-28.33, 3.34) * mm});
            skLineSegment(sketch, "E38.3.0", {"start": v(-23.55, -9.41) * mm, "end": v(-20.8, -8.62) * mm});
            skPoint(sketch, "E38.3.1", {"position": v(-20.48, -8.53) * mm});
            skLineSegment(sketch, "E38.3.2", {"start": v(-24.93, -4.63) * mm, "end": v(-22.19, -3.84) * mm});
            skPoint(sketch, "E38.3.3", {"position": v(-27.32, -8.23) * mm});
            skArc(sketch, "E38.3.4", {"start": v(-23.55, -9.41) * mm, "mid": v(-25.46, -9.14) * mm, "end": v(-27.2, -8.3) * mm});
            skPoint(sketch, "E38.3.5", {"position": v(-21.86, -3.74) * mm});
            skArc(sketch, "E38.3.6", {"start": v(-24.93, -4.63) * mm, "mid": v(-26.4, -5.88) * mm, "end": v(-27.43, -7.52) * mm});
            skPoint(sketch, "E38.3.7", {"position": v(-27.49, -7.64) * mm});
            skArc(sketch, "E38.3.8", {"start": v(-27.36, -8.1) * mm, "mid": v(-27.3, -8.22) * mm, "end": v(-27.2, -8.3) * mm});
            skLineSegment(sketch, "E38.3.9", {"start": v(-27.36, -8.1) * mm, "end": v(-27.4, -7.94) * mm});
            skArc(sketch, "E38.3.10", {"start": v(-20.35, -8.83) * mm, "mid": v(-20.53, -8.64) * mm, "end": v(-20.8, -8.62) * mm});
            skArc(sketch, "E38.3.11", {"start": v(-22.19, -3.84) * mm, "mid": v(-21.97, -3.67) * mm, "end": v(-21.92, -3.41) * mm});
            skLineSegment(sketch, "E38.3.12", {"start": v(-27.45, -7.77) * mm, "end": v(-27.4, -7.94) * mm});
            skArc(sketch, "E38.3.13", {"start": v(-27.43, -7.52) * mm, "mid": v(-27.46, -7.64) * mm, "end": v(-27.45, -7.77) * mm});
            skLineSegment(sketch, "E38.4.0", {"start": v(-18.15, -17.72) * mm, "end": v(-15.92, -15.94) * mm});
            skPoint(sketch, "E38.4.1", {"position": v(-15.65, -15.73) * mm});
            skLineSegment(sketch, "E38.4.2", {"start": v(-21.26, -13.83) * mm, "end": v(-19.03, -12.05) * mm});
            skPoint(sketch, "E38.4.3", {"position": v(-22.09, -18.07) * mm});
            skArc(sketch, "E38.4.4", {"start": v(-18.15, -17.72) * mm, "mid": v(-20.02, -18.2) * mm, "end": v(-21.95, -18.1) * mm});
            skPoint(sketch, "E38.4.5", {"position": v(-18.76, -11.84) * mm});
            skArc(sketch, "E38.4.6", {"start": v(-21.26, -13.83) * mm, "mid": v(-22.14, -15.55) * mm, "end": v(-22.47, -17.46) * mm});
            skPoint(sketch, "E38.4.7", {"position": v(-22.47, -17.6) * mm});
            skArc(sketch, "E38.4.8", {"start": v(-22.17, -17.97) * mm, "mid": v(-22.07, -18.06) * mm, "end": v(-21.95, -18.1) * mm});
            skLineSegment(sketch, "E38.4.9", {"start": v(-22.17, -17.97) * mm, "end": v(-22.28, -17.84) * mm});
            skArc(sketch, "E38.4.10", {"start": v(-15.41, -15.97) * mm, "mid": v(-15.66, -15.86) * mm, "end": v(-15.92, -15.94) * mm});
            skArc(sketch, "E38.4.11", {"start": v(-19.03, -12.05) * mm, "mid": v(-18.89, -11.82) * mm, "end": v(-18.94, -11.56) * mm});
            skLineSegment(sketch, "E38.4.12", {"start": v(-22.38, -17.7) * mm, "end": v(-22.28, -17.84) * mm});
            skArc(sketch, "E38.4.13", {"start": v(-22.47, -17.46) * mm, "mid": v(-22.45, -17.59) * mm, "end": v(-22.38, -17.7) * mm});
            skLineSegment(sketch, "E38.5.0", {"start": v(-9.98, -23.34) * mm, "end": v(-8.6, -20.84) * mm});
            skPoint(sketch, "E38.5.1", {"position": v(-8.44, -20.54) * mm});
            skLineSegment(sketch, "E38.5.2", {"start": v(-14.34, -20.93) * mm, "end": v(-12.96, -18.43) * mm});
            skPoint(sketch, "E38.5.3", {"position": v(-13.49, -25.17) * mm});
            skArc(sketch, "E38.5.4", {"start": v(-9.98, -23.34) * mm, "mid": v(-11.53, -24.5) * mm, "end": v(-13.35, -25.14) * mm});
            skPoint(sketch, "E38.5.5", {"position": v(-12.8, -18.14) * mm});
            skArc(sketch, "E38.5.6", {"start": v(-14.34, -20.93) * mm, "mid": v(-14.5, -22.86) * mm, "end": v(-14.07, -24.75) * mm});
            skPoint(sketch, "E38.5.7", {"position": v(-14.02, -24.87) * mm});
            skArc(sketch, "E38.5.8", {"start": v(-13.6, -25.1) * mm, "mid": v(-13.48, -25.15) * mm, "end": v(-13.35, -25.14) * mm});
            skLineSegment(sketch, "E38.5.9", {"start": v(-13.6, -25.1) * mm, "end": v(-13.75, -25.02) * mm});
            skArc(sketch, "E38.5.10", {"start": v(-8.13, -20.67) * mm, "mid": v(-8.4, -20.66) * mm, "end": v(-8.6, -20.84) * mm});
            skArc(sketch, "E38.5.11", {"start": v(-12.96, -18.43) * mm, "mid": v(-12.92, -18.17) * mm, "end": v(-13.07, -17.94) * mm});
            skLineSegment(sketch, "E38.5.12", {"start": v(-13.9, -24.94) * mm, "end": v(-13.75, -25.02) * mm});
            skArc(sketch, "E38.5.13", {"start": v(-14.07, -24.75) * mm, "mid": v(-14, -24.86) * mm, "end": v(-13.9, -24.94) * mm});
            skLineSegment(sketch, "E38.6.0", {"start": v(-0.29, -25.4) * mm, "end": v(0.03, -22.56) * mm});
            skPoint(sketch, "E38.6.1", {"position": v(0.07, -22.22) * mm});
            skLineSegment(sketch, "E38.6.2", {"start": v(-5.23, -24.84) * mm, "end": v(-4.92, -22) * mm});
            skPoint(sketch, "E38.6.3", {"position": v(-2.82, -28.43) * mm});
            skArc(sketch, "E38.6.4", {"start": v(-0.29, -25.4) * mm, "mid": v(-1.27, -27.06) * mm, "end": v(-2.7, -28.36) * mm});
            skPoint(sketch, "E38.6.5", {"position": v(-4.88, -21.67) * mm});
            skArc(sketch, "E38.6.6", {"start": v(-5.23, -24.84) * mm, "mid": v(-4.64, -26.69) * mm, "end": v(-3.52, -28.27) * mm});
            skPoint(sketch, "E38.6.7", {"position": v(-3.43, -28.36) * mm});
            skArc(sketch, "E38.6.8", {"start": v(-2.96, -28.42) * mm, "mid": v(-2.83, -28.4) * mm, "end": v(-2.7, -28.36) * mm});
            skLineSegment(sketch, "E38.6.9", {"start": v(-2.96, -28.42) * mm, "end": v(-3.13, -28.4) * mm});
            skArc(sketch, "E38.6.10", {"start": v(0.4, -22.22) * mm, "mid": v(0.15, -22.32) * mm, "end": v(0.03, -22.56) * mm});
            skArc(sketch, "E38.6.11", {"start": v(-4.92, -22) * mm, "mid": v(-4.98, -21.75) * mm, "end": v(-5.2, -21.6) * mm});
            skLineSegment(sketch, "E38.6.12", {"start": v(-3.3, -28.38) * mm, "end": v(-3.13, -28.4) * mm});
            skArc(sketch, "E38.6.13", {"start": v(-3.52, -28.27) * mm, "mid": v(-3.42, -28.34) * mm, "end": v(-3.3, -28.38) * mm});
            skLineSegment(sketch, "E38.7.0", {"start": v(9.46, -23.6) * mm, "end": v(8.67, -20.85) * mm});
            skPoint(sketch, "E38.7.1", {"position": v(8.57, -20.52) * mm});
            skLineSegment(sketch, "E38.7.2", {"start": v(4.68, -24.97) * mm, "end": v(3.88, -22.23) * mm});
            skPoint(sketch, "E38.7.3", {"position": v(8.27, -27.36) * mm});
            skArc(sketch, "E38.7.4", {"start": v(9.46, -23.6) * mm, "mid": v(9.19, -25.5) * mm, "end": v(8.35, -27.25) * mm});
            skPoint(sketch, "E38.7.5", {"position": v(3.79, -21.9) * mm});
            skArc(sketch, "E38.7.6", {"start": v(4.68, -24.97) * mm, "mid": v(5.93, -26.45) * mm, "end": v(7.56, -27.48) * mm});
            skPoint(sketch, "E38.7.7", {"position": v(7.7, -27.53) * mm});
            skArc(sketch, "E38.7.8", {"start": v(8.15, -27.4) * mm, "mid": v(8.26, -27.35) * mm, "end": v(8.35, -27.25) * mm});
            skLineSegment(sketch, "E38.7.9", {"start": v(8.15, -27.4) * mm, "end": v(7.98, -27.45) * mm});
            skArc(sketch, "E38.7.10", {"start": v(8.88, -20.4) * mm, "mid": v(8.69, -20.58) * mm, "end": v(8.67, -20.85) * mm});
            skArc(sketch, "E38.7.11", {"start": v(3.88, -22.23) * mm, "mid": v(3.72, -22.02) * mm, "end": v(3.46, -21.96) * mm});
            skLineSegment(sketch, "E38.7.12", {"start": v(7.82, -27.5) * mm, "end": v(7.98, -27.45) * mm});
            skArc(sketch, "E38.7.13", {"start": v(7.56, -27.48) * mm, "mid": v(7.69, -27.51) * mm, "end": v(7.82, -27.5) * mm});
            skLineSegment(sketch, "E38.8.0", {"start": v(17.77, -18.2) * mm, "end": v(15.99, -15.96) * mm});
            skPoint(sketch, "E38.8.1", {"position": v(15.78, -15.7) * mm});
            skLineSegment(sketch, "E38.8.2", {"start": v(13.88, -21.3) * mm, "end": v(12.1, -19.07) * mm});
            skPoint(sketch, "E38.8.3", {"position": v(18.12, -22.13) * mm});
            skArc(sketch, "E38.8.4", {"start": v(17.77, -18.2) * mm, "mid": v(18.25, -20.07) * mm, "end": v(18.15, -22) * mm});
            skPoint(sketch, "E38.8.5", {"position": v(11.89, -18.8) * mm});
            skArc(sketch, "E38.8.6", {"start": v(13.88, -21.3) * mm, "mid": v(15.6, -22.19) * mm, "end": v(17.5, -22.51) * mm});
            skPoint(sketch, "E38.8.7", {"position": v(17.65, -22.51) * mm});
            skArc(sketch, "E38.8.8", {"start": v(18.02, -22.22) * mm, "mid": v(18.1, -22.12) * mm, "end": v(18.15, -22) * mm});
            skLineSegment(sketch, "E38.8.9", {"start": v(18.02, -22.22) * mm, "end": v(17.88, -22.33) * mm});
            skArc(sketch, "E38.8.10", {"start": v(16.01, -15.46) * mm, "mid": v(15.9, -15.7) * mm, "end": v(15.99, -15.96) * mm});
            skArc(sketch, "E38.8.11", {"start": v(12.1, -19.07) * mm, "mid": v(11.87, -18.93) * mm, "end": v(11.6, -18.98) * mm});
            skLineSegment(sketch, "E38.8.12", {"start": v(17.75, -22.43) * mm, "end": v(17.88, -22.33) * mm});
            skArc(sketch, "E38.8.13", {"start": v(17.5, -22.51) * mm, "mid": v(17.64, -22.5) * mm, "end": v(17.75, -22.43) * mm});
            skLineSegment(sketch, "E38.9.0", {"start": v(23.38, -10.03) * mm, "end": v(20.88, -8.65) * mm});
            skPoint(sketch, "E38.9.1", {"position": v(20.59, -8.48) * mm});
            skLineSegment(sketch, "E38.9.2", {"start": v(20.98, -14.39) * mm, "end": v(18.48, -13) * mm});
            skPoint(sketch, "E38.9.3", {"position": v(25.21, -13.53) * mm});
            skArc(sketch, "E38.9.4", {"start": v(23.38, -10.03) * mm, "mid": v(24.55, -11.57) * mm, "end": v(25.2, -13.4) * mm});
            skPoint(sketch, "E38.9.5", {"position": v(18.18, -12.85) * mm});
            skArc(sketch, "E38.9.6", {"start": v(20.98, -14.39) * mm, "mid": v(22.9, -14.55) * mm, "end": v(24.8, -14.12) * mm});
            skPoint(sketch, "E38.9.7", {"position": v(24.92, -14.06) * mm});
            skArc(sketch, "E38.9.8", {"start": v(25.15, -13.65) * mm, "mid": v(25.2, -13.53) * mm, "end": v(25.2, -13.4) * mm});
            skLineSegment(sketch, "E38.9.9", {"start": v(25.15, -13.65) * mm, "end": v(25.07, -13.8) * mm});
            skArc(sketch, "E38.9.10", {"start": v(20.71, -8.17) * mm, "mid": v(20.7, -8.44) * mm, "end": v(20.88, -8.65) * mm});
            skArc(sketch, "E38.9.11", {"start": v(18.48, -13) * mm, "mid": v(18.21, -12.97) * mm, "end": v(17.99, -13.12) * mm});
            skLineSegment(sketch, "E38.9.12", {"start": v(24.99, -13.95) * mm, "end": v(25.07, -13.8) * mm});
            skArc(sketch, "E38.9.13", {"start": v(24.8, -14.12) * mm, "mid": v(24.9, -14.05) * mm, "end": v(24.99, -13.95) * mm});
            skLineSegment(sketch, "E38.10.0", {"start": v(25.44, -0.33) * mm, "end": v(22.6, -0.02) * mm});
            skPoint(sketch, "E38.10.1", {"position": v(22.27, 0.02) * mm});
            skLineSegment(sketch, "E38.10.2", {"start": v(24.9, -5.28) * mm, "end": v(22.05, -4.96) * mm});
            skPoint(sketch, "E38.10.3", {"position": v(28.48, -2.87) * mm});
            skArc(sketch, "E38.10.4", {"start": v(25.44, -0.33) * mm, "mid": v(27.11, -1.32) * mm, "end": v(28.4, -2.76) * mm});
            skPoint(sketch, "E38.10.5", {"position": v(21.72, -4.93) * mm});
            skArc(sketch, "E38.10.6", {"start": v(24.9, -5.28) * mm, "mid": v(26.73, -4.69) * mm, "end": v(28.31, -3.57) * mm});
            skPoint(sketch, "E38.10.7", {"position": v(28.4, -3.47) * mm});
            skArc(sketch, "E38.10.8", {"start": v(28.46, -3) * mm, "mid": v(28.45, -2.87) * mm, "end": v(28.4, -2.76) * mm});
            skLineSegment(sketch, "E38.10.9", {"start": v(28.46, -3) * mm, "end": v(28.45, -3.17) * mm});
            skArc(sketch, "E38.10.10", {"start": v(22.27, 0.36) * mm, "mid": v(22.37, 0.1) * mm, "end": v(22.6, -0.02) * mm});
            skArc(sketch, "E38.10.11", {"start": v(22.05, -4.96) * mm, "mid": v(21.8, -5.03) * mm, "end": v(21.64, -5.25) * mm});
            skLineSegment(sketch, "E38.10.12", {"start": v(28.43, -3.34) * mm, "end": v(28.45, -3.17) * mm});
            skArc(sketch, "E38.10.13", {"start": v(28.31, -3.57) * mm, "mid": v(28.39, -3.47) * mm, "end": v(28.43, -3.34) * mm});
            skLineSegment(sketch, "E38.11.0", {"start": v(23.64, 9.41) * mm, "end": v(20.9, 8.62) * mm});
            skPoint(sketch, "E38.11.1", {"position": v(20.57, 8.53) * mm});
            skLineSegment(sketch, "E38.11.2", {"start": v(25.02, 4.63) * mm, "end": v(22.28, 3.84) * mm});
            skPoint(sketch, "E38.11.3", {"position": v(27.41, 8.23) * mm});
            skArc(sketch, "E38.11.4", {"start": v(23.64, 9.41) * mm, "mid": v(25.55, 9.14) * mm, "end": v(27.3, 8.3) * mm});
            skPoint(sketch, "E38.11.5", {"position": v(21.95, 3.74) * mm});
            skArc(sketch, "E38.11.6", {"start": v(25.02, 4.63) * mm, "mid": v(26.5, 5.88) * mm, "end": v(27.53, 7.52) * mm});
            skPoint(sketch, "E38.11.7", {"position": v(27.58, 7.64) * mm});
            skArc(sketch, "E38.11.8", {"start": v(27.45, 8.1) * mm, "mid": v(27.4, 8.22) * mm, "end": v(27.3, 8.3) * mm});
            skLineSegment(sketch, "E38.11.9", {"start": v(27.45, 8.1) * mm, "end": v(27.5, 7.94) * mm});
            skArc(sketch, "E38.11.10", {"start": v(20.44, 8.83) * mm, "mid": v(20.63, 8.64) * mm, "end": v(20.9, 8.62) * mm});
            skArc(sketch, "E38.11.11", {"start": v(22.28, 3.84) * mm, "mid": v(22.06, 3.67) * mm, "end": v(22, 3.41) * mm});
            skLineSegment(sketch, "E38.11.12", {"start": v(27.54, 7.77) * mm, "end": v(27.5, 7.94) * mm});
            skArc(sketch, "E38.11.13", {"start": v(27.53, 7.52) * mm, "mid": v(27.56, 7.64) * mm, "end": v(27.54, 7.77) * mm});
            skLineSegment(sketch, "E38.12.0", {"start": v(18.24, 17.72) * mm, "end": v(16.01, 15.94) * mm});
            skPoint(sketch, "E38.12.1", {"position": v(15.75, 15.73) * mm});
            skLineSegment(sketch, "E38.12.2", {"start": v(21.35, 13.83) * mm, "end": v(19.12, 12.05) * mm});
            skPoint(sketch, "E38.12.3", {"position": v(22.18, 18.07) * mm});
            skArc(sketch, "E38.12.4", {"start": v(18.24, 17.72) * mm, "mid": v(20.11, 18.2) * mm, "end": v(22.05, 18.1) * mm});
            skPoint(sketch, "E38.12.5", {"position": v(18.85, 11.84) * mm});
            skArc(sketch, "E38.12.6", {"start": v(21.35, 13.83) * mm, "mid": v(22.23, 15.55) * mm, "end": v(22.56, 17.46) * mm});
            skPoint(sketch, "E38.12.7", {"position": v(22.56, 17.6) * mm});
            skArc(sketch, "E38.12.8", {"start": v(22.26, 17.97) * mm, "mid": v(22.17, 18.06) * mm, "end": v(22.05, 18.1) * mm});
            skLineSegment(sketch, "E38.12.9", {"start": v(22.26, 17.97) * mm, "end": v(22.37, 17.84) * mm});
            skArc(sketch, "E38.12.10", {"start": v(15.5, 15.97) * mm, "mid": v(15.75, 15.86) * mm, "end": v(16.01, 15.94) * mm});
            skArc(sketch, "E38.12.11", {"start": v(19.12, 12.05) * mm, "mid": v(18.98, 11.82) * mm, "end": v(19.03, 11.56) * mm});
            skLineSegment(sketch, "E38.12.12", {"start": v(22.48, 17.7) * mm, "end": v(22.37, 17.84) * mm});
            skArc(sketch, "E38.12.13", {"start": v(22.56, 17.46) * mm, "mid": v(22.54, 17.59) * mm, "end": v(22.48, 17.7) * mm});
            skLineSegment(sketch, "E38.13.0", {"start": v(10.07, 23.34) * mm, "end": v(8.7, 20.84) * mm});
            skPoint(sketch, "E38.13.1", {"position": v(8.53, 20.54) * mm});
            skLineSegment(sketch, "E38.13.2", {"start": v(14.43, 20.93) * mm, "end": v(13.05, 18.43) * mm});
            skPoint(sketch, "E38.13.3", {"position": v(13.58, 25.17) * mm});
            skArc(sketch, "E38.13.4", {"start": v(10.07, 23.34) * mm, "mid": v(11.62, 24.5) * mm, "end": v(13.44, 25.14) * mm});
            skPoint(sketch, "E38.13.5", {"position": v(12.9, 18.14) * mm});
            skArc(sketch, "E38.13.6", {"start": v(14.43, 20.93) * mm, "mid": v(14.6, 22.86) * mm, "end": v(14.16, 24.75) * mm});
            skPoint(sketch, "E38.13.7", {"position": v(14.11, 24.87) * mm});
            skArc(sketch, "E38.13.8", {"start": v(13.7, 25.1) * mm, "mid": v(13.57, 25.15) * mm, "end": v(13.44, 25.14) * mm});
            skLineSegment(sketch, "E38.13.9", {"start": v(13.7, 25.1) * mm, "end": v(13.85, 25.02) * mm});
            skArc(sketch, "E38.13.10", {"start": v(8.22, 20.67) * mm, "mid": v(8.49, 20.66) * mm, "end": v(8.7, 20.84) * mm});
            skArc(sketch, "E38.13.11", {"start": v(13.05, 18.43) * mm, "mid": v(13.02, 18.17) * mm, "end": v(13.16, 17.94) * mm});
            skLineSegment(sketch, "E38.13.12", {"start": v(14, 24.94) * mm, "end": v(13.85, 25.02) * mm});
            skArc(sketch, "E38.13.13", {"start": v(14.16, 24.75) * mm, "mid": v(14.1, 24.86) * mm, "end": v(14, 24.94) * mm});
            skLineSegment(sketch, "E38.14.0", {"start": v(0.38, 25.4) * mm, "end": v(0.06, 22.56) * mm});
            skPoint(sketch, "E38.14.1", {"position": v(0.02, 22.22) * mm});
            skLineSegment(sketch, "E38.14.2", {"start": v(5.33, 24.84) * mm, "end": v(5.01, 22) * mm});
            skPoint(sketch, "E38.14.3", {"position": v(2.92, 28.43) * mm});
            skArc(sketch, "E38.14.4", {"start": v(0.38, 25.4) * mm, "mid": v(1.36, 27.06) * mm, "end": v(2.8, 28.36) * mm});
            skPoint(sketch, "E38.14.5", {"position": v(4.97, 21.67) * mm});
            skArc(sketch, "E38.14.6", {"start": v(5.33, 24.84) * mm, "mid": v(4.74, 26.69) * mm, "end": v(3.62, 28.27) * mm});
            skPoint(sketch, "E38.14.7", {"position": v(3.52, 28.36) * mm});
            skArc(sketch, "E38.14.8", {"start": v(3.05, 28.42) * mm, "mid": v(2.92, 28.4) * mm, "end": v(2.8, 28.36) * mm});
            skLineSegment(sketch, "E38.14.9", {"start": v(3.05, 28.42) * mm, "end": v(3.22, 28.4) * mm});
            skArc(sketch, "E38.14.10", {"start": v(-0.31, 22.22) * mm, "mid": v(-0.06, 22.32) * mm, "end": v(0.06, 22.56) * mm});
            skArc(sketch, "E38.14.11", {"start": v(5.01, 22) * mm, "mid": v(5.08, 21.75) * mm, "end": v(5.3, 21.6) * mm});
            skLineSegment(sketch, "E38.14.12", {"start": v(3.39, 28.38) * mm, "end": v(3.22, 28.4) * mm});
            skArc(sketch, "E38.14.13", {"start": v(3.62, 28.27) * mm, "mid": v(3.51, 28.34) * mm, "end": v(3.39, 28.38) * mm});
            skLineSegment(sketch, "E38.15.0", {"start": v(-9.37, 23.6) * mm, "end": v(-8.57, 20.85) * mm});
            skPoint(sketch, "E38.15.1", {"position": v(-8.48, 20.52) * mm});
            skLineSegment(sketch, "E38.15.2", {"start": v(-4.58, 24.97) * mm, "end": v(-3.79, 22.23) * mm});
            skPoint(sketch, "E38.15.3", {"position": v(-8.18, 27.36) * mm});
            skArc(sketch, "E38.15.4", {"start": v(-9.37, 23.6) * mm, "mid": v(-9.1, 25.5) * mm, "end": v(-8.26, 27.25) * mm});
            skPoint(sketch, "E38.15.5", {"position": v(-3.7, 21.9) * mm});
            skArc(sketch, "E38.15.6", {"start": v(-4.58, 24.97) * mm, "mid": v(-5.83, 26.45) * mm, "end": v(-7.47, 27.48) * mm});
            skPoint(sketch, "E38.15.7", {"position": v(-7.6, 27.53) * mm});
            skArc(sketch, "E38.15.8", {"start": v(-8.05, 27.4) * mm, "mid": v(-8.17, 27.35) * mm, "end": v(-8.26, 27.25) * mm});
            skLineSegment(sketch, "E38.15.9", {"start": v(-8.05, 27.4) * mm, "end": v(-7.9, 27.45) * mm});
            skArc(sketch, "E38.15.10", {"start": v(-8.79, 20.4) * mm, "mid": v(-8.6, 20.58) * mm, "end": v(-8.57, 20.85) * mm});
            skArc(sketch, "E38.15.11", {"start": v(-3.79, 22.23) * mm, "mid": v(-3.63, 22.02) * mm, "end": v(-3.36, 21.96) * mm});
            skLineSegment(sketch, "E38.15.12", {"start": v(-7.72, 27.5) * mm, "end": v(-7.9, 27.45) * mm});
            skArc(sketch, "E38.15.13", {"start": v(-7.47, 27.48) * mm, "mid": v(-7.6, 27.51) * mm, "end": v(-7.72, 27.5) * mm});
            skArc(sketch, "E39.trimOffspring", {"start": v(-8.48, 20.52) * mm, "mid": v(-10.02, 19.81) * mm, "end": v(-11.5, 18.98) * mm});
            skArc(sketch, "E40.trimOffspring", {"start": v(-20.5, 8.48) * mm, "mid": v(-21.14, 6.73) * mm, "end": v(-21.63, 4.93) * mm});
            skArc(sketch, "E41.trimOffspring", {"start": v(0.02, 22.22) * mm, "mid": v(-1.84, 22.14) * mm, "end": v(-3.7, 21.9) * mm});
            skArc(sketch, "E42.trimOffspring", {"start": v(-22.18, -0.02) * mm, "mid": v(-22.1, -1.89) * mm, "end": v(-21.86, -3.74) * mm});
            skArc(sketch, "E43.trimOffspring", {"start": v(-20.48, -8.53) * mm, "mid": v(-19.77, -10.07) * mm, "end": v(-18.94, -11.56) * mm});
            skArc(sketch, "E44.trimOffspring", {"start": v(8.53, 20.54) * mm, "mid": v(6.78, 21.18) * mm, "end": v(4.97, 21.67) * mm});
            skArc(sketch, "E45.trimOffspring", {"start": v(15.75, 15.73) * mm, "mid": v(14.37, 17) * mm, "end": v(12.9, 18.14) * mm});
            skArc(sketch, "E46.trimOffspring", {"start": v(-15.65, -15.73) * mm, "mid": v(-14.4, -16.89) * mm, "end": v(-13.07, -17.94) * mm});
            skArc(sketch, "E47.trimOffspring", {"start": v(-8.44, -20.54) * mm, "mid": v(-6.68, -21.18) * mm, "end": v(-4.88, -21.67) * mm});
            skArc(sketch, "E48.trimOffspring", {"start": v(8.57, -20.52) * mm, "mid": v(10.27, -19.74) * mm, "end": v(11.89, -18.8) * mm});
            skArc(sketch, "E49.trimOffspring", {"start": v(0.07, -22.22) * mm, "mid": v(1.94, -22.14) * mm, "end": v(3.79, -21.9) * mm});
            skArc(sketch, "E50.trimOffspring", {"start": v(15.78, -15.7) * mm, "mid": v(16.93, -14.45) * mm, "end": v(17.99, -13.12) * mm});
            skArc(sketch, "E51.trimOffspring", {"start": v(20.59, -8.48) * mm, "mid": v(21.18, -6.89) * mm, "end": v(21.64, -5.25) * mm});
            skArc(sketch, "E52.trimOffspring", {"start": v(22.27, 0.02) * mm, "mid": v(22.2, 1.89) * mm, "end": v(21.95, 3.74) * mm});
            skArc(sketch, "E53.trimOffspring", {"start": v(20.57, 8.53) * mm, "mid": v(19.78, 10.22) * mm, "end": v(18.85, 11.84) * mm});
            skSolve(sketch);
        }
        {
            var Q0;
            Q0=makeQuery(id+"F2.imprint","IMPRINT",FACE,{"disambiguationData":[TD([[makeQuery(id+"F2.imprint","IMPRINT",EDGE,{"derivedFrom":sQuery(id+"F2.wireOp",EDGE,"E28.trimOffspring")}),1.0]])]});
            var Q1;
            Q1=makeQuery(id+"F0.imprint","IMPRINT",FACE,{"disambiguationData":[TD([[makeQuery(id+"F0.imprint","IMPRINT",EDGE,{"derivedFrom":sQuery(id+"F0.wireOp",EDGE,"E1.trimOffspring")}),1.0]])]});
            var Q2;
            Q2=sQuery(id+"F0.wireOp",VERTEX,"E6.MirrorCS.start");
            var Q3;
            Q3=sQuery(id+"F2.wireOp",VERTEX,"E38.13.4.start");
            loft(context, id + "F3", {"sheetProfilesArray" : [{ "sheetProfileEntities" : qUnion([Q0]) }, { "sheetProfileEntities" : qUnion([Q1]) }], "matchConnections" : true, "connections" : [{ "connectionEntities" : qUnion([Q2, Q3]), "connectionEdgeQueries" : qUnion([]), "connectionEdgeParameters" : [] }]});
        }
        {
            var Q0;
            Q0=makeQuery(id+"F3.opLoft","CAP_FACE",FACE,{"disambiguationData":[OSD([makeQuery(id+"F2.imprint","IMPRINT",FACE,{"disambiguationData":[TD([[makeQuery(id+"F2.imprint","IMPRINT",EDGE,{"derivedFrom":sQuery(id+"F2.wireOp",EDGE,"E28.trimOffspring")}),1.0]])]})])],"isStart":true});
            var sketch = newSketch(context, id + "F4", { "sketchPlane" : qUnion([Q0])});
            skCircle(sketch, "E54", {"center": v(0, 0) * mm, "radius": 6.35 * mm});
            skSolve(sketch);
        }
        {
            var Q0;
            Q0=qSketchRegion(id+"F4",true);
            extrude(context, id + "F5", {"entities" : qUnion([Q0]), "operationType" : NewBodyOperationType.REMOVE, "oppositeDirection" : true, "depth" : 50.8 * mm});
        }
    });
